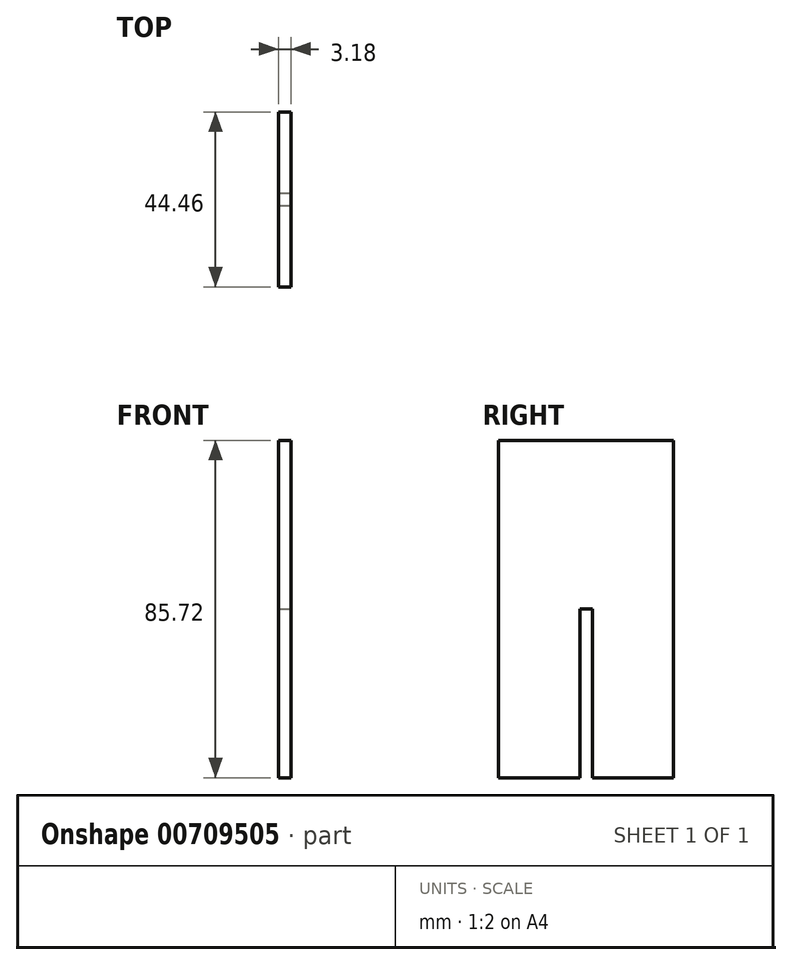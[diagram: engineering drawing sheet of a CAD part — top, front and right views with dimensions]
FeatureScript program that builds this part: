
annotation { "Feature Type Name" : "Feature", "Feature Type Description" : "" }
export const myFeature = defineFeature(function(context is Context, id is Id, definition is map)
    precondition{}
    {
        {
            var Q0;
            Q0=qCreatedBy(makeId("Right.planeOp"),FACE);
            var sketch = newSketch(context, id + "F0", { "sketchPlane" : qUnion([Q0])});
            skLineSegment(sketch, "E0.bottom", {"start": v(-22.22, 42.86) * mm, "end": v(22.23, 42.86) * mm});
            skLineSegment(sketch, "E0.top", {"start": v(-22.23, -42.86) * mm, "end": v(22.22, -42.86) * mm});
            skLineSegment(sketch, "E0.left", {"start": v(-22.22, 42.86) * mm, "end": v(-22.23, -42.86) * mm});
            skLineSegment(sketch, "E0.right", {"start": v(22.23, 42.86) * mm, "end": v(22.22, -42.86) * mm});
            skPoint(sketch, "E0.middle", {"position": v(0, 0) * mm});
            skSolve(sketch);
        }
        {
            var Q0;
            Q0=makeQuery(id+"F0.imprint","IMPRINT",FACE,{"disambiguationData":[TD([[makeQuery(id+"F0.imprint","IMPRINT",EDGE,{"derivedFrom":sQuery(id+"F0.wireOp",EDGE,"E0.bottom")}),-1.0]])]});
            extrude(context, id + "F1", {"entities" : qUnion([Q0]), "depth" : 3.17 * mm, "offsetDistance" : 25.4 * mm});
        }
        {
            var Q0;
            Q0=makeQuery(id+"F1.opExtrude","CAP_FACE",FACE,{"disambiguationData":[OSD([sQuery(id+"F0.wireOp",EDGE,"E0.bottom"),sQuery(id+"F0.wireOp",EDGE,"E0.top"),sQuery(id+"F0.wireOp",EDGE,"E0.left"),sQuery(id+"F0.wireOp",EDGE,"E0.right")])],"isStart":false});
            var sketch = newSketch(context, id + "F2", { "sketchPlane" : qUnion([Q0])});
            skLineSegment(sketch, "E1.bottom", {"start": v(1.57, -42.86) * mm, "end": v(-1.6, -42.86) * mm});
            skLineSegment(sketch, "E1.top", {"start": v(1.57, 0.01) * mm, "end": v(-1.6, 0.01) * mm});
            skLineSegment(sketch, "E1.left", {"start": v(1.57, -42.86) * mm, "end": v(1.57, 0.01) * mm});
            skLineSegment(sketch, "E1.right", {"start": v(-1.6, -42.86) * mm, "end": v(-1.6, 0.01) * mm});
            skSolve(sketch);
        }
        {
            var Q0;
            Q0=makeQuery(id+"F2.imprint","IMPRINT",FACE,{"disambiguationData":[TD([[makeQuery(id+"F2.imprint","IMPRINT",EDGE,{"derivedFrom":sQuery(id+"F2.wireOp",EDGE,"E1.bottom")}),1.0]])]});
            extrude(context, id + "F3", {"entities" : qUnion([Q0]), "operationType" : NewBodyOperationType.REMOVE, "oppositeDirection" : true, "depth" : 25.4 * mm, "offsetDistance" : 25.4 * mm});
        }
    });
